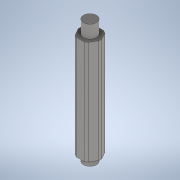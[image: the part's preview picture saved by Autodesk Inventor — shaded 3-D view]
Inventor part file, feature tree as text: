
AUTODESK INVENTOR PART (.ipt)
format: ipt  version: 2020 (Build 240168000, 168)  size: 146,432 bytes
history: native  units: in
note: dims shown in document units (in); Inventor stores cm internally (conversion verified against a paired STEP export)
features: extrude x3, sketch x3, projected_geometry x2
ambient origin geometry x8: Origin, YZ Plane, XZ Plane, XY Plane, X Axis, Y Axis, Z Axis, Center Point
bodies: Solid1 (feature_tree)
feature tree (8):
  extrude  "Extrusion1"  Depth=0.375in
  extrude  "Extrusion2"  Depth=0.25in
  extrude  "Extrusion3"  Depth=0.25in
  sketch  "Sketch1"  dims[d0=0.375in d1=0.4035in]
  sketch  "Sketch2"  dims[d2=2.375in d3=0.0in d4=0.25in]
  projected_geometry  "Projected Loop1"
  sketch  "Sketch3"  dims[d5=0.125in d6=0.0in d7=0.25in d8=0.25in d9=0.0in]
  projected_geometry  "Projected Loop2"
